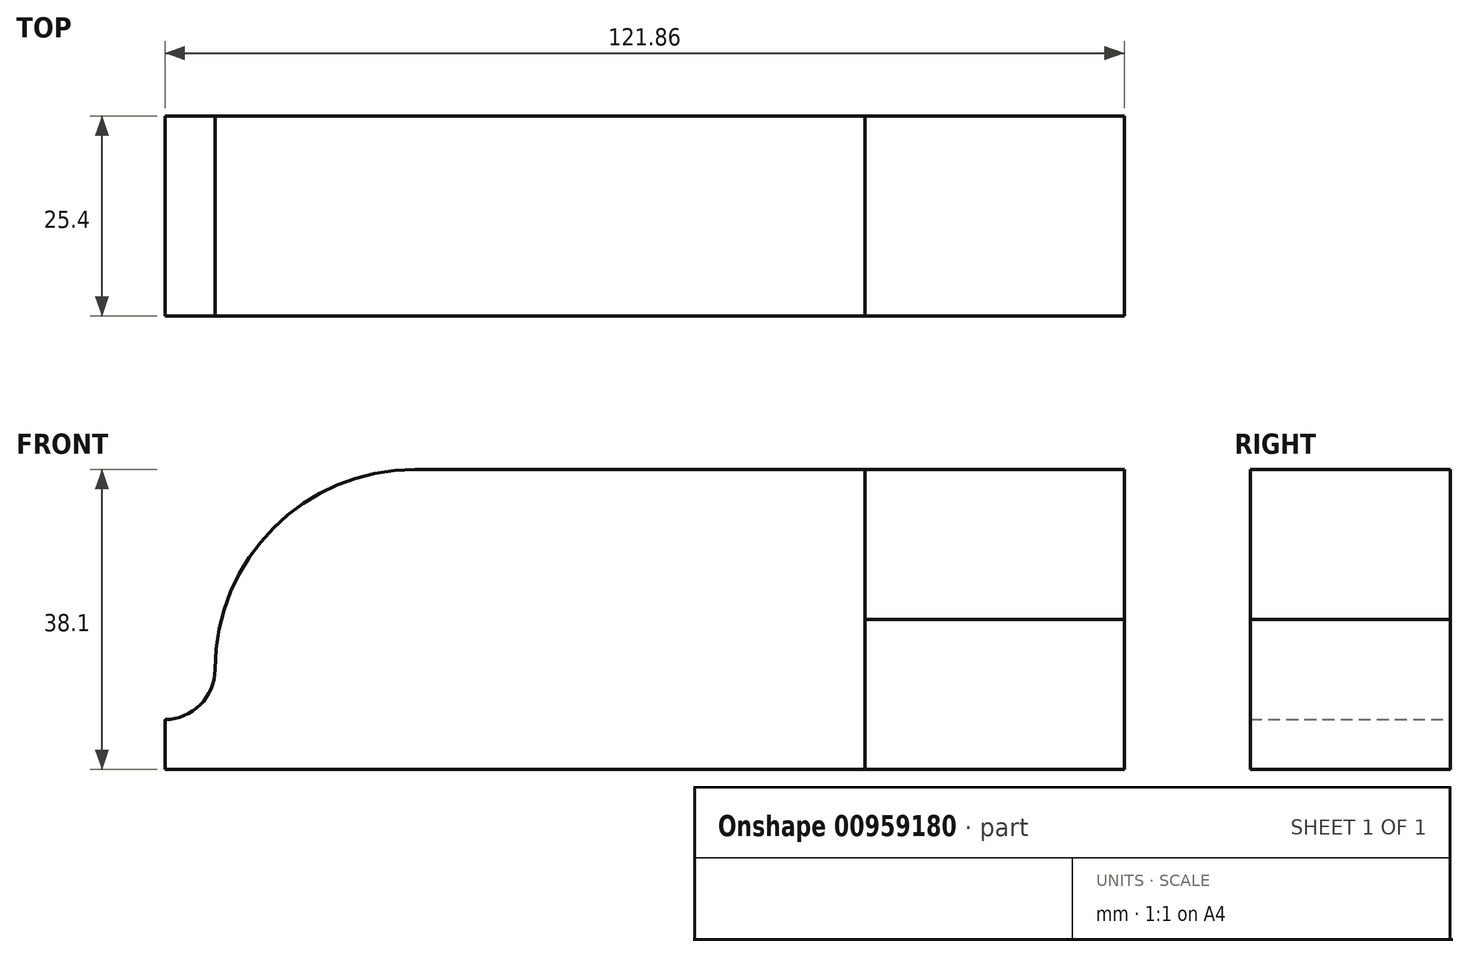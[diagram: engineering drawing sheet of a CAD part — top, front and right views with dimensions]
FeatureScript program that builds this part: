
annotation { "Feature Type Name" : "Feature", "Feature Type Description" : "" }
export const myFeature = defineFeature(function(context is Context, id is Id, definition is map)
    precondition{}
    {
        {
            var Q0;
            Q0=qCreatedBy(makeId("Front.planeOp"),FACE);
            var sketch = newSketch(context, id + "F0", { "sketchPlane" : qUnion([Q0])});
            skLineSegment(sketch, "E0", {"start": v(0, 0) * mm, "end": v(-72.9, 0) * mm});
            skLineSegment(sketch, "E1", {"start": v(-72.9, 0) * mm, "end": v(-72.9, 6.35) * mm});
            skLineSegment(sketch, "E2", {"start": v(-72.9, 6.35) * mm, "end": v(-72.9, 6.35) * mm});
            skLineSegment(sketch, "E3", {"start": v(-66.55, 12.7) * mm, "end": v(-66.55, 12.7) * mm});
            skLineSegment(sketch, "E4", {"start": v(-41.15, 38.1) * mm, "end": v(16, 38.1) * mm});
            skLineSegment(sketch, "E5", {"start": v(3.36, 0) * mm, "end": v(48.96, 0) * mm});
            skLineSegment(sketch, "E6", {"start": v(48.96, 0) * mm, "end": v(48.96, 38.1) * mm});
            skLineSegment(sketch, "E7", {"start": v(48.96, 38.1) * mm, "end": v(16, 38.1) * mm});
            skPoint(sketch, "E8.visualSharp", {"position": v(-66.55, 38.1) * mm});
            skArc(sketch, "E8.filletArc", {"start": v(-41.15, 38.1) * mm, "mid": v(-59.1, 30.66) * mm, "end": v(-66.55, 12.7) * mm});
            skPoint(sketch, "E9.visualSharp", {"position": v(-66.55, 6.35) * mm});
            skArc(sketch, "E9.filletArc", {"start": v(-72.9, 6.35) * mm, "mid": v(-68.4, 8.2) * mm, "end": v(-66.55, 12.7) * mm});
            skLineSegment(sketch, "E10", {"start": v(0, 0) * mm, "end": v(3.36, 0) * mm});
            skLineSegment(sketch, "E11", {"start": v(16, 19.05) * mm, "end": v(51.88, 19.05) * mm});
            skLineSegment(sketch, "E12", {"start": v(16, 38.1) * mm, "end": v(16, 0) * mm});
            skSolve(sketch);
        }
        {
            var Q0;
            Q0=makeQuery(id+"F0.imprint","IMPRINT",FACE,{"disambiguationData":[TD([[makeQuery(id+"F0.imprint","IMPRINT",EDGE,{"derivedFrom":sQuery(id+"F0.wireOp",EDGE,"E0")}),-1.0]])]});
            extrude(context, id + "F1", {"entities" : qUnion([Q0]), "depth" : 25.4 * mm, "offsetDistance" : 25.4 * mm});
        }
        {
            var Q0;
            {var subQ0=sQuery(id+"F0.wireOp",EDGE,"E7");Q0=makeQuery(id+"F0.imprint","IMPRINT",FACE,{"disambiguationData":[TD([[makeQuery(id+"F0.imprint","IMPRINT",EDGE,{"derivedFrom":subQ0}),1.0]])]});}
            extrude(context, id + "F2", {"entities" : qUnion([Q0]), "depth" : 25.4 * mm, "offsetDistance" : 25.4 * mm});
        }
        {
            var Q0;
            {var subQ0=sQuery(id+"F0.wireOp",EDGE,"E6");var subQ1=sQuery(id+"F0.wireOp",EDGE,"E5");var subQ2=makeQuery(id+"F0.imprint","INTERSECT",VERTEX,{"derivedFrom":[subQ1,subQ0]});Q0=makeQuery(id+"F0.imprint","IMPRINT",FACE,{"disambiguationData":[TD([[makeQuery(id+"F0.imprint","IMPRINT",EDGE,{"disambiguationData":[TD([[subQ2,1.0]])],"derivedFrom":subQ1}),1.0]])]});}
            extrude(context, id + "F3", {"entities" : qUnion([Q0]), "depth" : 25.4 * mm, "offsetDistance" : 25.4 * mm});
        }
    });
